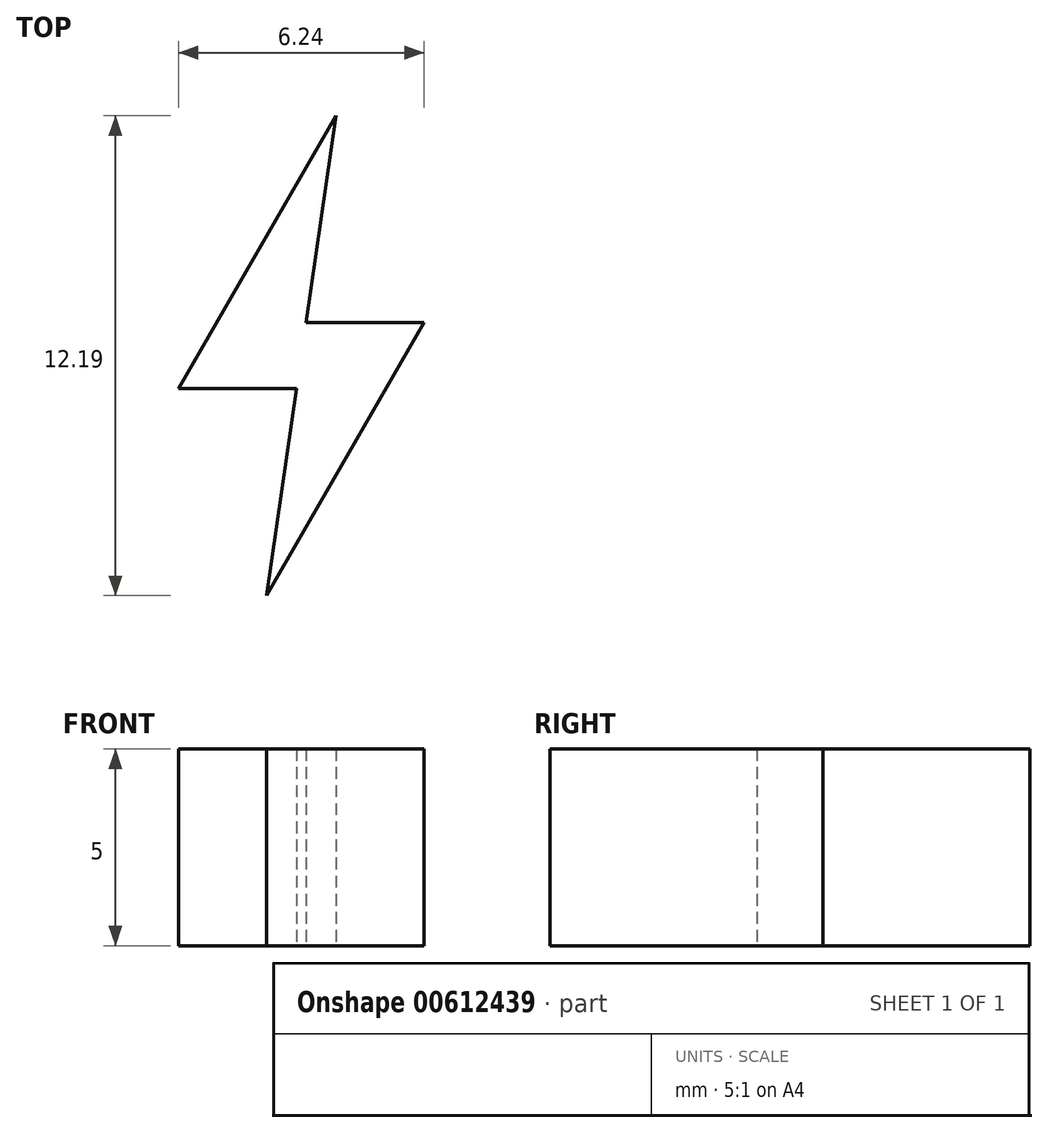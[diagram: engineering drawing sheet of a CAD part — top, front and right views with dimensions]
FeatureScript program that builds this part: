
annotation { "Feature Type Name" : "Feature", "Feature Type Description" : "" }
export const myFeature = defineFeature(function(context is Context, id is Id, definition is map)
    precondition{}
    {
        {
            var Q0;
            Q0=qCreatedBy(makeId("Top.planeOp"),FACE);
            var sketch = newSketch(context, id + "F0", { "sketchPlane" : qUnion([Q0])});
            skLineSegment(sketch, "E0", {"start": v(0, 0) * mm, "end": v(-3, 0) * mm});
            skLineSegment(sketch, "E1", {"start": v(-3, 0) * mm, "end": v(1, 6.93) * mm});
            skLineSegment(sketch, "E2", {"start": v(1, 6.93) * mm, "end": v(0, 0) * mm});
            skLineSegment(sketch, "E3", {"start": v(0.24, 1.67) * mm, "end": v(3.24, 1.67) * mm});
            skLineSegment(sketch, "E4", {"start": v(3.24, 1.67) * mm, "end": v(-0.76, -5.26) * mm});
            skLineSegment(sketch, "E5", {"start": v(-0.76, -5.26) * mm, "end": v(0.24, 1.67) * mm});
            skSolve(sketch);
        }
        {
            var Q0;
            Q0=makeQuery(id+"F0.imprint","IMPRINT",FACE,{"disambiguationData":[TD([[makeQuery(id+"F0.imprint","IMPRINT",EDGE,{"derivedFrom":sQuery(id+"F0.wireOp",EDGE,"E3")}),-1.0]])]});
            var Q1;
            Q1=makeQuery(id+"F0.imprint","IMPRINT",FACE,{"disambiguationData":[TD([[makeQuery(id+"F0.imprint","IMPRINT",EDGE,{"derivedFrom":sQuery(id+"F0.wireOp",EDGE,"E0")}),-1.0]])]});
            extrude(context, id + "F1", {"entities" : qUnion([Q0, Q1]), "depth" : 5 * mm, "offsetDistance" : 25 * mm});
        }
    });
